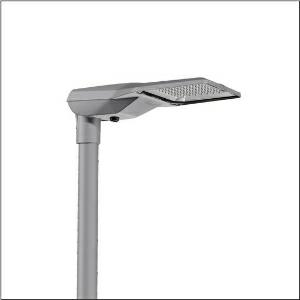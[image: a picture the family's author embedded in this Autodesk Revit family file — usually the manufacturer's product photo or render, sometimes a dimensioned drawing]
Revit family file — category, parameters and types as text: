
# Revit family: streetlight_sl_21_midi___p0_5a_5xe3v33r08lb_9200
name_source: partatom
category: Lighting Fixtures
units: mm (PartAtom-declared; Revit-internal decimal feet)

## family parameters
Cut with Voids When Loaded = No
Host = Face
Light Source = No
Part Type = Normal
Room Calculation Point = No
Round Connector Dimension = Use Diameter
Shared = No

## types (1)
- --- (1 x LED, 14100 lm, 99.6 W, 3000K)
    Apparent Load = 100 VA
    CIE Flux Codes = 37 73 96 100 100
    Color Rendering = 70
    Color Temperature = 3000K
    Default Elevation = 1800 mm
    Description = Streetlight SL 21 midi, mast luminaire, primary light control with lens, of PMMA, primary optical cover: cover, of toughened safety glass, transparent, light distribution: P0.5a, light emission: direct distribution, primary light characteristic: asymmetric, installation type: post-top, side-entry, LED, High Power LED, rated luminous flux: 14.100lm, luminous efficacy: 142lm/W, light colour: 730, colour temperature: 3000K, control gear: D4i, control: pre-setting: logarithmic dimming characteristic, flexible luminous flux parameterisation, time-dependent luminous flux control, constant luminous flux control, overheat protection, mains connection: 230..240V, AC, 50/60Hz, start of lifetime: 100W, end of service life: 102W, reduction: 46W, luminaire housing, of diecast aluminium, powder-coated, SITECO metallic grey (DB 702S), corrosivity category C5 high according to DIN EN ISO 12944, multi-level sealing system, sealing non-destructively replaceable, inclination adjustable: 0°, 5°, 10°, 15°, please order mast flange separately, length: 644mm, width: 335mm, height: 110mm, mast flange for spigot size: 42mm (side-entry): 5XC10008XM4, 60/48mm (side-entry/post-top): 5XC10108XM2, 76/60mm (side-entry/post-top): 5XC10108XM1, mounting height: 4..8m, Smart Interface below, protection rating (complete): IP66, insulation class (complete): insulation class II (safety insulation), certification: CE, ENEC, ENEC+, VDE, impact resistance: IK10, permissible operating ambient temperature for outdoor applications: -40..+50°C, standard-compliant lighting for roads and squares, packaging unit: 1 piece

Light Distribution: P0.5a
    Height = 111 mm
    Lamp = 1 x LED
    Lamp Light Flux = 14100 lm
    Lamp Power = 99.6 W
    Lamp count = 1
    Length = 644 mm
    Luminous efficacy = 142 lm/W
    Manufacturer = Siteco
    ModVariant = No
    Model = 5XE3V33R08LB
    Number of Poles = 1
    OnlyDefault = Yes
    Power Factor = 1
    Product Name = Streetlight SL 21 midi | P0.5a
    Product group = mast luminaire | pylon top
    ProductGroupID = 6100
    Protection Class = Protection class II
    Protection Degree = IP 66
    RLX_Detail_Level = 1
    RLX_Emergency_Light_Flux = 0 lm
    RLX_Emergency_Type = 0
    RLX_Emergency_Type_DB = No
    RlxData = <blob elided: 26425 chars, md5=eabf00f6>
    Socket = socket
    Standby Power = 0 W
    System Light Flux = 14100 lm
    System Power = 100 W
    Type Comments = factory setting: luminous flux: 100 % | dim-lin: 254 | 1020 mA
    Type Image = l_1004300.jpg
    URL = http://relux.com
    VarID = @adj_032887
    Voltage = 0 V
    Weight = 0.00 kg
    Width = 336 mm

## geometry (parser evidence)
native form markers: Blend x4, Sweep x11
no freeform markers — native parametric forms only
